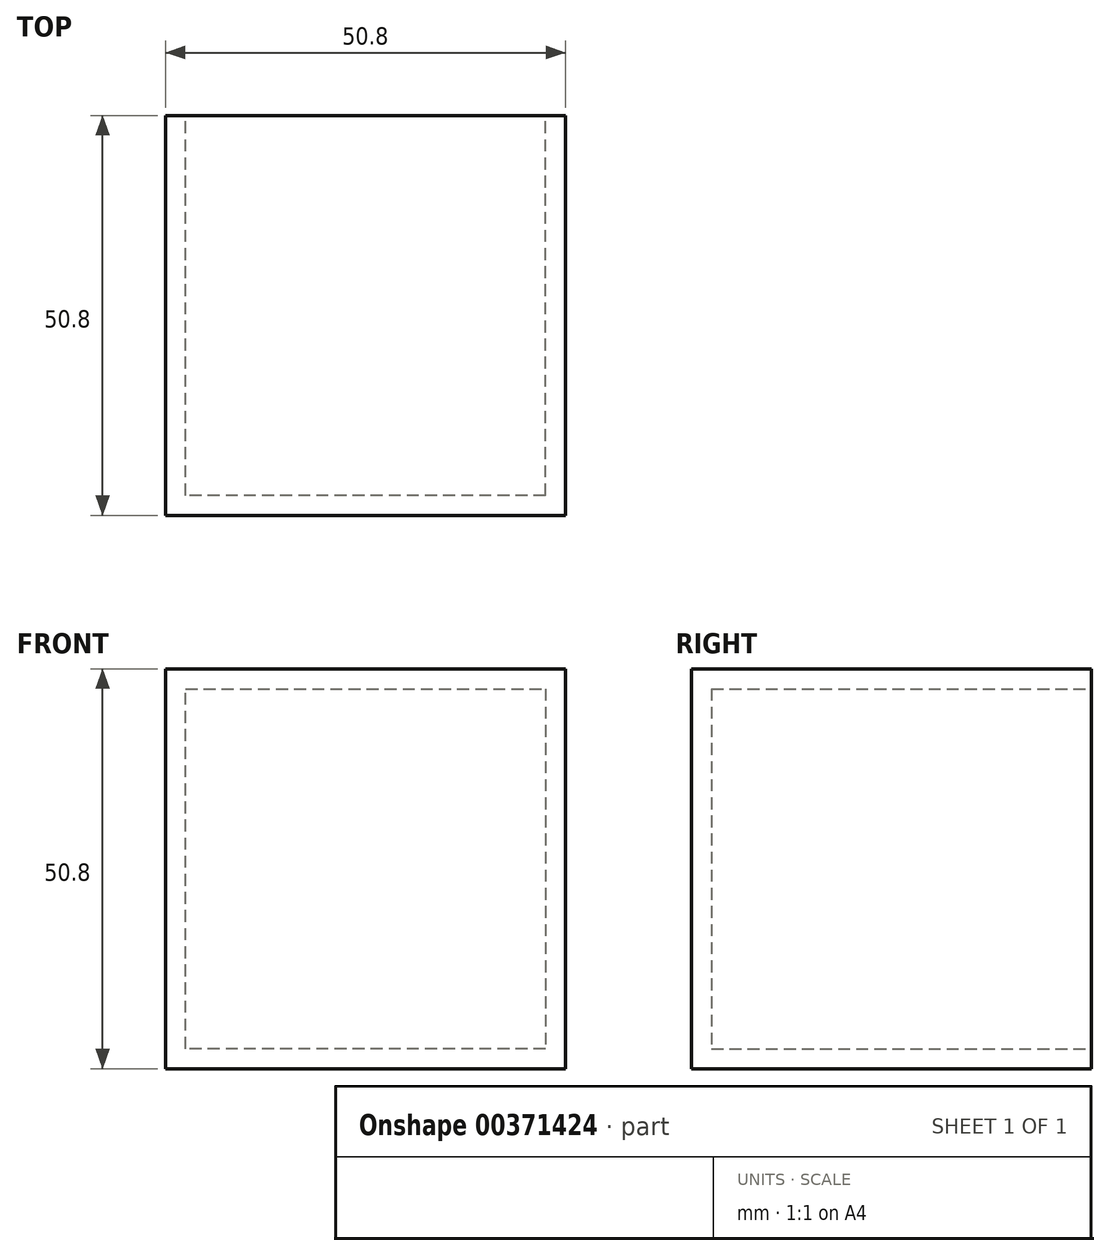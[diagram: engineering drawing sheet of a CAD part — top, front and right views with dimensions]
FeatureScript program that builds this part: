
annotation { "Feature Type Name" : "Feature", "Feature Type Description" : "" }
export const myFeature = defineFeature(function(context is Context, id is Id, definition is map)
    precondition{}
    {
        {
            var Q0;
            Q0=qCreatedBy(makeId("Front.planeOp"),FACE);
            var sketch = newSketch(context, id + "F0", { "sketchPlane" : qUnion([Q0])});
            skLineSegment(sketch, "E0.bottom", {"start": v(-25.4, 25.4) * mm, "end": v(25.4, 25.4) * mm});
            skLineSegment(sketch, "E0.top", {"start": v(-25.4, -25.4) * mm, "end": v(25.4, -25.4) * mm});
            skLineSegment(sketch, "E0.left", {"start": v(-25.4, 25.4) * mm, "end": v(-25.4, -25.4) * mm});
            skLineSegment(sketch, "E0.right", {"start": v(25.4, 25.4) * mm, "end": v(25.4, -25.4) * mm});
            skPoint(sketch, "E0.middle", {"position": v(0, 0) * mm});
            skSolve(sketch);
        }
        {
            var Q0;
            Q0=makeQuery(id+"F0.imprint","IMPRINT",FACE,{"disambiguationData":[TD([[makeQuery(id+"F0.imprint","IMPRINT",EDGE,{"derivedFrom":sQuery(id+"F0.wireOp",EDGE,"E0.bottom")}),-1.0]])]});
            extrude(context, id + "F1", {"entities" : qUnion([Q0]), "depth" : 50.8 * mm});
        }
        {
            var Q0;
            Q0=makeQuery(id+"F1.opExtrude","CAP_FACE",FACE,{"disambiguationData":[OSD([sQuery(id+"F0.wireOp",EDGE,"E0.bottom"),sQuery(id+"F0.wireOp",EDGE,"E0.top"),sQuery(id+"F0.wireOp",EDGE,"E0.left"),sQuery(id+"F0.wireOp",EDGE,"E0.right")])],"isStart":true});
            shell(context, id + "F2", {"entities" : qUnion([Q0]), "thickness" : 2.54 * mm});
        }
        {
            var Q0;
            Q0=qCreatedBy(makeId("Front.planeOp"),FACE);
            var sketch = newSketch(context, id + "F3", { "sketchPlane" : qUnion([Q0])});
            skLineSegment(sketch, "E1.0.0", {"start": v(-22.86, -22.86) * mm, "end": v(-22.86, 22.86) * mm});
            skLineSegment(sketch, "E1.0.1", {"start": v(-22.86, 22.86) * mm, "end": v(22.86, 22.86) * mm});
            skLineSegment(sketch, "E1.0.2", {"start": v(22.86, 22.86) * mm, "end": v(22.86, -22.86) * mm});
            skLineSegment(sketch, "E1.0.3", {"start": v(22.86, -22.86) * mm, "end": v(-22.86, -22.86) * mm});
            skSolve(sketch);
        }
        {
            var Q0;
            Q0=makeQuery(id+"F3.imprint","IMPRINT",FACE,{"disambiguationData":[TD([[makeQuery(id+"F3.imprint","IMPRINT",EDGE,{"derivedFrom":sQuery(id+"F3.wireOp",EDGE,"E1.0.0")}),-1.0]])]});
            var Q1;
            Q1=makeQuery(id+"F2.opShell","OFFSET_FACE",FACE,{"disambiguationData":[OSD([sQuery(id+"F0.wireOp",EDGE,"E0.bottom"),sQuery(id+"F0.wireOp",EDGE,"E0.top"),sQuery(id+"F0.wireOp",EDGE,"E0.left"),sQuery(id+"F0.wireOp",EDGE,"E0.right")])]});
            extrude(context, id + "F4", {"entities" : qUnion([Q0]), "endBound" : BoundingType.UP_TO_SURFACE, "endBoundEntityFace" : qUnion([Q1]), "depth" : 25.4 * mm});
        }
    });
